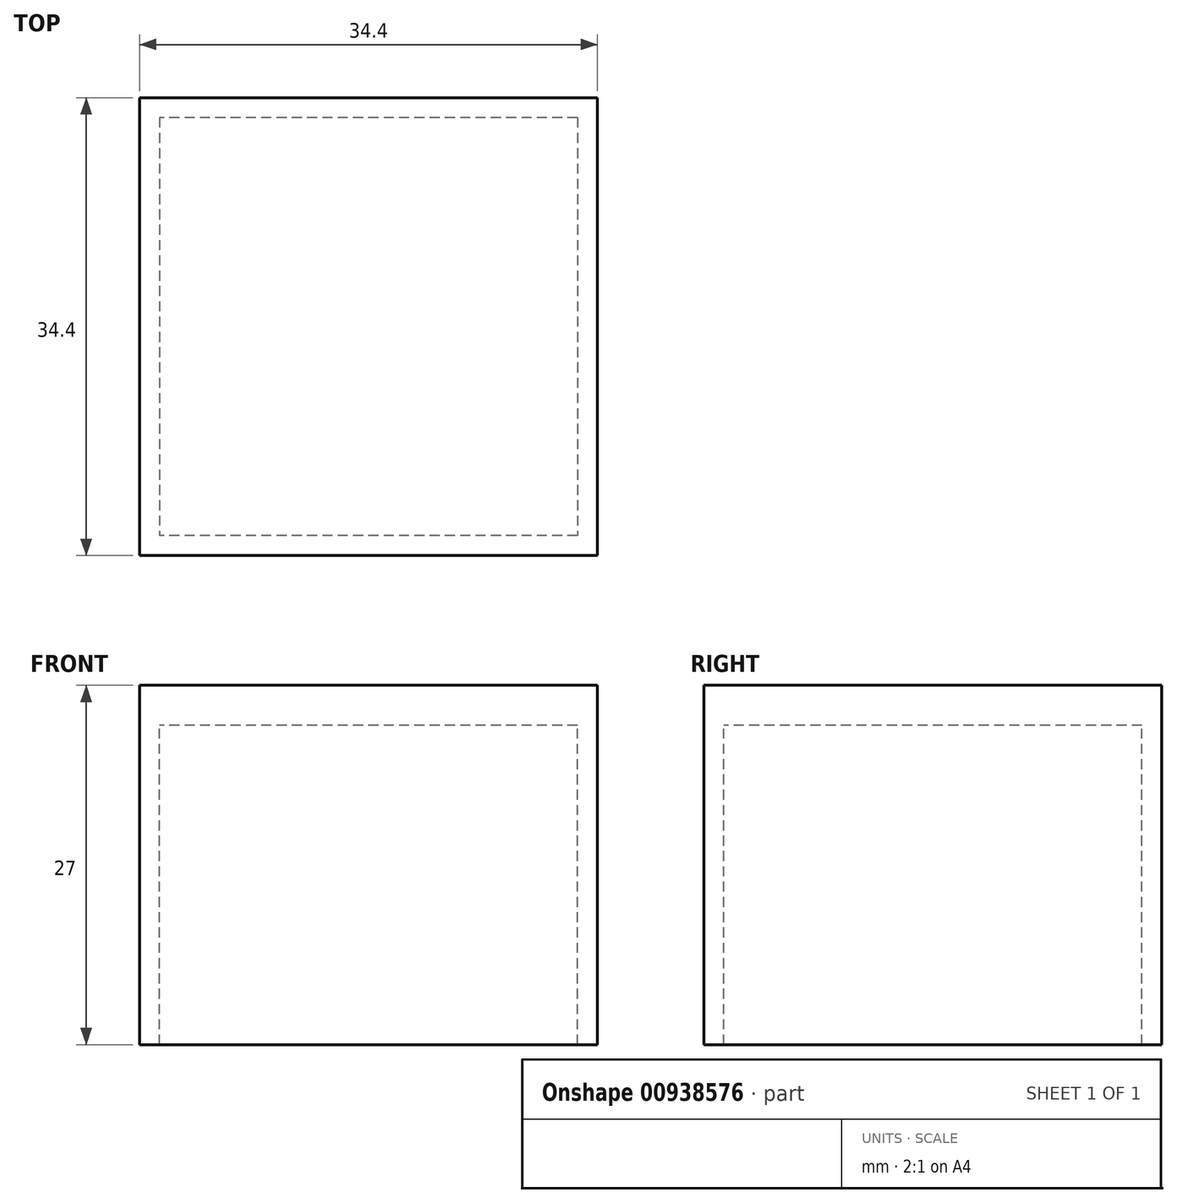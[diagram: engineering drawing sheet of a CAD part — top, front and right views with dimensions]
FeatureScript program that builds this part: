
annotation { "Feature Type Name" : "Feature", "Feature Type Description" : "" }
export const myFeature = defineFeature(function(context is Context, id is Id, definition is map)
    precondition{}
    {
        {
            var Q0;
            Q0=qCreatedBy(makeId("Top.planeOp"),FACE);
            var sketch = newSketch(context, id + "F0", { "sketchPlane" : qUnion([Q0])});
            skLineSegment(sketch, "E0.bottom", {"start": v(17.2, 17.2) * mm, "end": v(-17.2, 17.2) * mm});
            skLineSegment(sketch, "E0.top", {"start": v(17.2, -17.2) * mm, "end": v(-17.2, -17.2) * mm});
            skLineSegment(sketch, "E0.left", {"start": v(17.2, 17.2) * mm, "end": v(17.2, -17.2) * mm});
            skLineSegment(sketch, "E0.right", {"start": v(-17.2, 17.2) * mm, "end": v(-17.2, -17.2) * mm});
            skPoint(sketch, "E0.middle", {"position": v(0, 0) * mm});
            skLineSegment(sketch, "E1.bottom", {"start": v(15.7, 15.7) * mm, "end": v(-15.7, 15.7) * mm});
            skLineSegment(sketch, "E1.top", {"start": v(15.7, -15.7) * mm, "end": v(-15.7, -15.7) * mm});
            skLineSegment(sketch, "E1.left", {"start": v(15.7, 15.7) * mm, "end": v(15.7, -15.7) * mm});
            skLineSegment(sketch, "E1.right", {"start": v(-15.7, 15.7) * mm, "end": v(-15.7, -15.7) * mm});
            skSolve(sketch);
        }
        {
            var Q0;
            Q0=makeQuery(id+"F0.imprint","IMPRINT",FACE,{"disambiguationData":[TD([[makeQuery(id+"F0.imprint","IMPRINT",EDGE,{"derivedFrom":sQuery(id+"F0.wireOp",EDGE,"E0.bottom")}),1.0]])]});
            extrude(context, id + "F1", {"entities" : qUnion([Q0]), "oppositeDirection" : true, "depth" : 27 * mm, "offsetDistance" : 25.4 * mm});
        }
        {
            var Q0;
            Q0=makeQuery(id+"F0.imprint","IMPRINT",FACE,{"disambiguationData":[TD([[makeQuery(id+"F0.imprint","IMPRINT",EDGE,{"derivedFrom":sQuery(id+"F0.wireOp",EDGE,"E1.bottom")}),1.0]])]});
            extrude(context, id + "F2", {"entities" : qUnion([Q0]), "operationType" : NewBodyOperationType.ADD, "oppositeDirection" : true, "depth" : 3 * mm, "offsetDistance" : 25.4 * mm});
        }
    });
